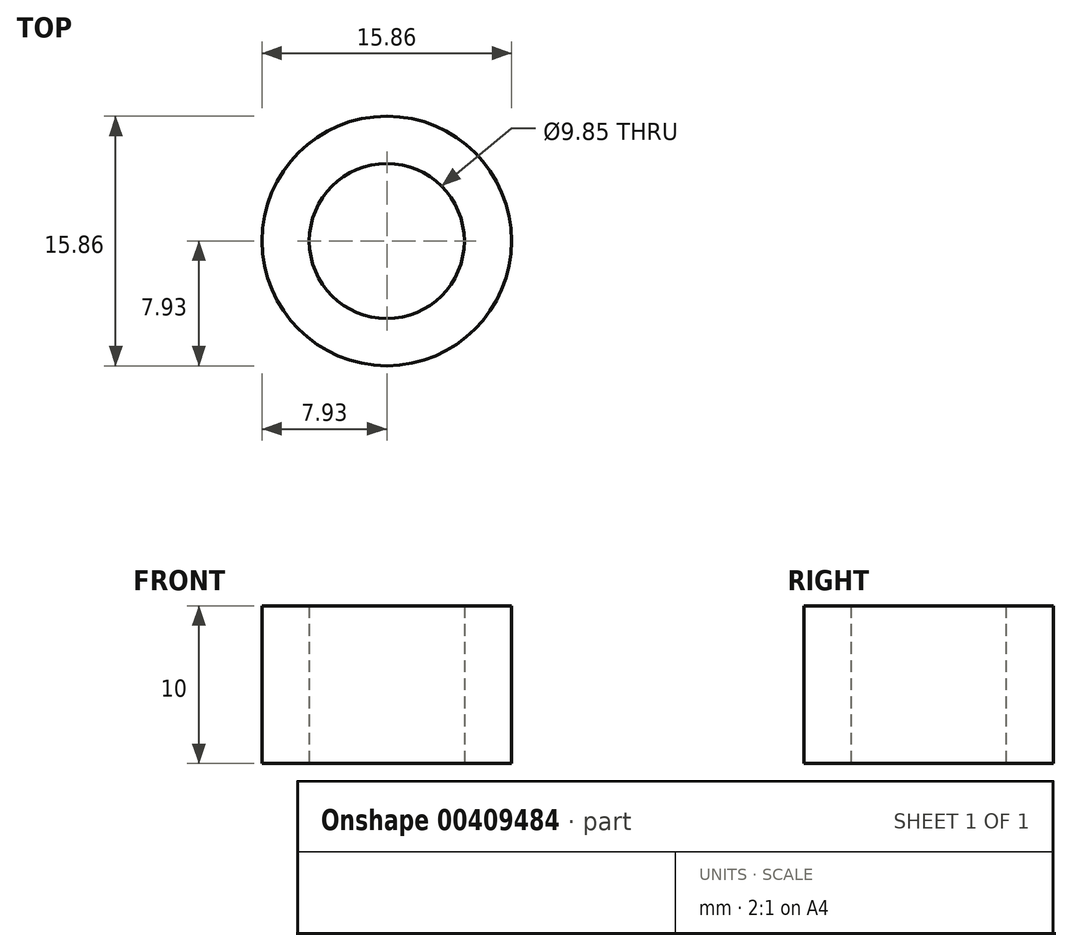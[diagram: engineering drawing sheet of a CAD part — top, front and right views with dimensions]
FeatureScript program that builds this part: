
annotation { "Feature Type Name" : "Feature", "Feature Type Description" : "" }
export const myFeature = defineFeature(function(context is Context, id is Id, definition is map)
    precondition{}
    {
        {
            var Q0;
            Q0=qCreatedBy(makeId("Top.planeOp"),FACE);
            var sketch = newSketch(context, id + "F0", { "sketchPlane" : qUnion([Q0])});
            skCircle(sketch, "E0", {"center": v(0, 0) * mm, "radius": 4.92 * mm});
            skCircle(sketch, "E1.0", {"center": v(0, 0) * mm, "radius": 7.92 * mm});
            skSolve(sketch);
        }
        {
            var Q0;
            Q0=makeQuery(id+"F0.imprint","IMPRINT",FACE,{"disambiguationData":[TD([[makeQuery(id+"F0.imprint","IMPRINT",EDGE,{"derivedFrom":sQuery(id+"F0.wireOp",EDGE,"E0")}),-1.0]])]});
            extrude(context, id + "F1", {"entities" : qUnion([Q0]), "depth" : 10 * mm});
        }
    });
